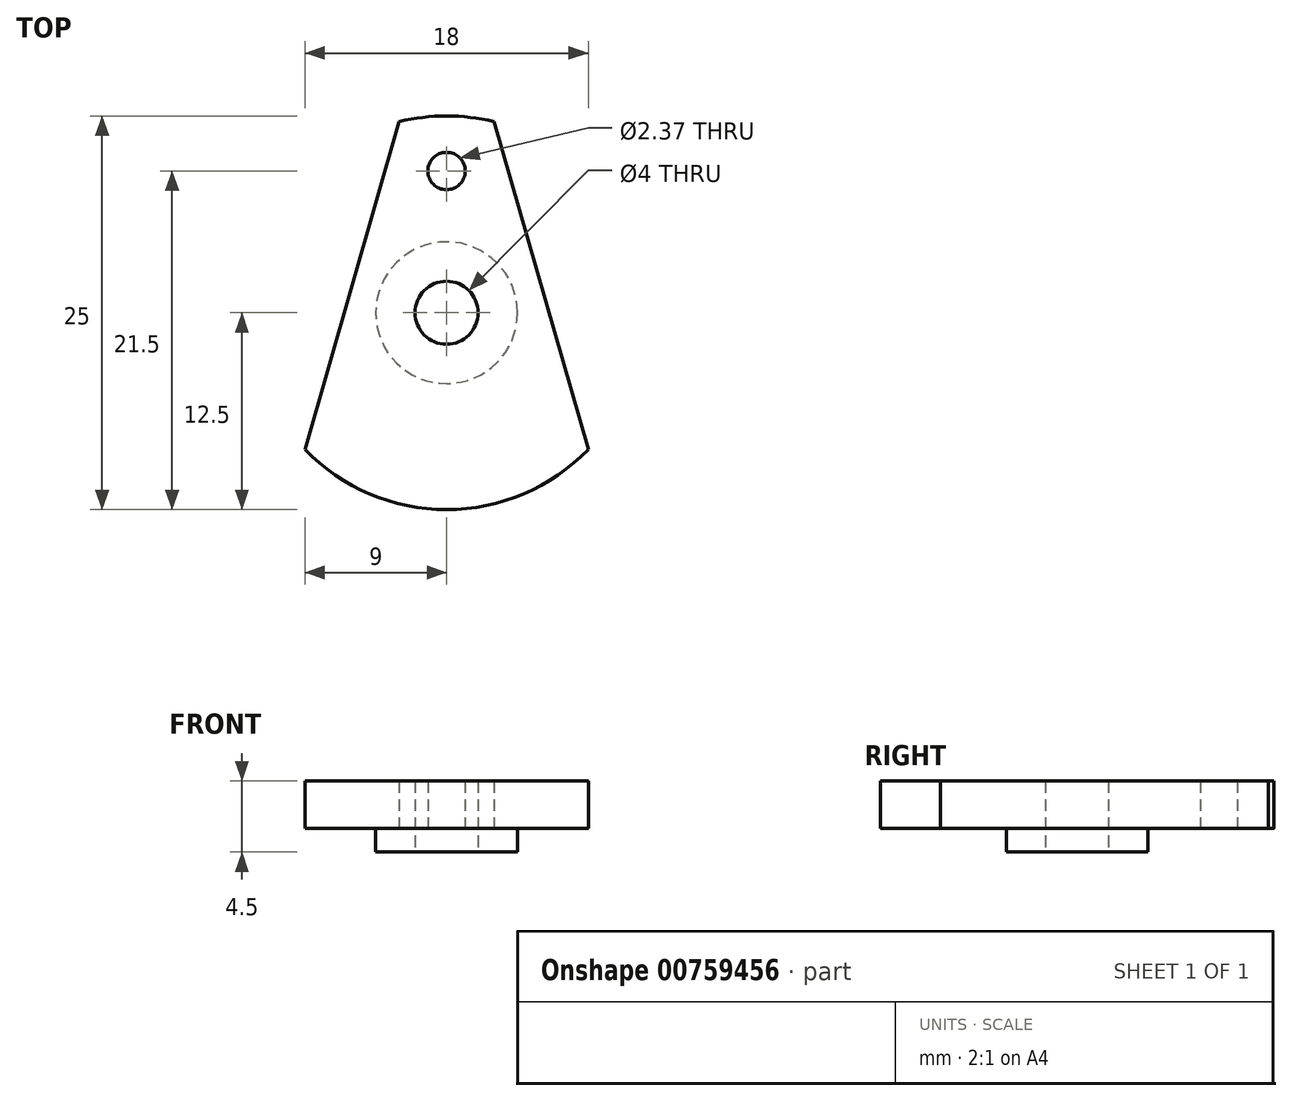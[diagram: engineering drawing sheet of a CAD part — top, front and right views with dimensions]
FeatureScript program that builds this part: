
annotation { "Feature Type Name" : "Feature", "Feature Type Description" : "" }
export const myFeature = defineFeature(function(context is Context, id is Id, definition is map)
    precondition{}
    {
        {
            var Q0;
            Q0=qCreatedBy(makeId("Top.planeOp"),FACE);
            var sketch = newSketch(context, id + "F0", { "sketchPlane" : qUnion([Q0])});
            skArc(sketch, "E0", {"start": v(3, 12.13) * mm, "mid": v(0, 12.5) * mm, "end": v(-3, 12.13) * mm});
            skCircle(sketch, "E1", {"center": v(0, 0) * mm, "radius": 2 * mm});
            skCircle(sketch, "E2", {"center": v(0, 0) * mm, "radius": 4.5 * mm});
            skLineSegment(sketch, "E3", {"start": v(3, 12.13) * mm, "end": v(9, -8.67) * mm});
            skLineSegment(sketch, "E4.MirrorCS", {"start": v(-3, 12.13) * mm, "end": v(-9, -8.67) * mm});
            skArc(sketch, "E5.trimOffspring", {"start": v(-9, -8.67) * mm, "mid": v(0, -12.5) * mm, "end": v(9, -8.67) * mm});
            skCircle(sketch, "E6", {"center": v(0, 9) * mm, "radius": 1.19 * mm});
            skSolve(sketch);
        }
        {
            var Q0;
            Q0=makeQuery(id+"F0.imprint","IMPRINT",FACE,{"disambiguationData":[TD([[makeQuery(id+"F0.imprint","IMPRINT",EDGE,{"derivedFrom":sQuery(id+"F0.wireOp",EDGE,"E0")}),1.0]])]});
            var Q1;
            Q1=makeQuery(id+"F0.imprint","IMPRINT",FACE,{"disambiguationData":[TD([[makeQuery(id+"F0.imprint","IMPRINT",EDGE,{"derivedFrom":sQuery(id+"F0.wireOp",EDGE,"E1")}),-1.0]])]});
            extrude(context, id + "F1", {"entities" : qUnion([Q0, Q1]), "depth" : 3 * mm, "offsetDistance" : 25 * mm});
        }
        {
            var Q0;
            Q0=makeQuery(id+"F0.imprint","IMPRINT",FACE,{"disambiguationData":[TD([[makeQuery(id+"F0.imprint","IMPRINT",EDGE,{"derivedFrom":sQuery(id+"F0.wireOp",EDGE,"E1")}),-1.0]])]});
            extrude(context, id + "F2", {"entities" : qUnion([Q0]), "operationType" : NewBodyOperationType.ADD, "oppositeDirection" : true, "depth" : 1.5 * mm, "offsetDistance" : 25 * mm});
        }
    });
